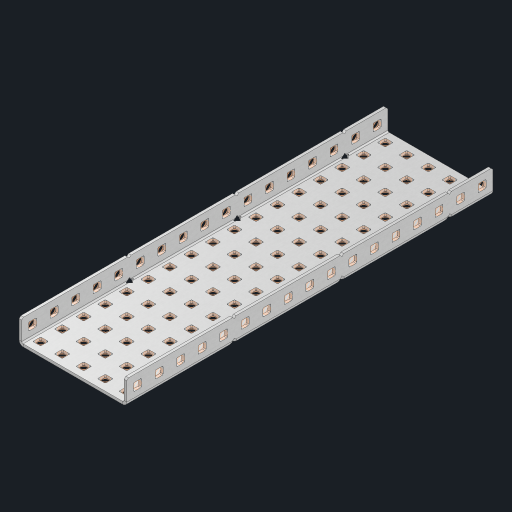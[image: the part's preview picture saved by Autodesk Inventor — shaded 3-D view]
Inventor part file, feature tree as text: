
AUTODESK INVENTOR PART (.ipt)
format: ipt  version: 2023 (Build 270158000, 158)  size: 1,488,896 bytes
history: native  units: in
note: dims shown in document units (in); Inventor stores cm internally (conversion verified against a paired STEP export)
features: other x124, extrude x118, sheet_metal_op x10, sketch x8, mirror x1, pattern_linear x1, chamfer x1
ambient origin geometry x8: Origin, YZ Plane, XZ Plane, XY Plane, X Axis, Y Axis, Z Axis, Center Point
bodies: Solid1 (feature_tree), Body (feature_tree)
feature tree (263):
  other  "Flange Pattern Plane"
  sheet_metal_op  "Flange Pattern"
  sheet_metal_op  "Body Pattern"
  other  "Arc Length"
  mirror  "Notch Mirror"
  pattern_linear  "Notch Pattern"  Spacing1=0.25in  [1 undecoded]
  chamfer  "End Chamfer"
  extrude  "Half Cut"  Depth=0.0625in
  sketch  "Sketch1"  dims[d0=2.5in]
  other  "Plate1"
  sketch  "Sketch2"  dims[d1=8.5in]
  other  "Plate2"
  sheet_metal_op  "Bend1"
  sheet_metal_op  "Corner1"
  sketch  "Sketch3"  dims[d2=0.0625in]
  other  "Flange Pattern Sketch"
  sketch  "Sketch7"  dims[d3=0.0625in]
  other  "Srf1"
  other  "Srf2"
  sketch  "Sketch8"  dims[d4=0.0312in]
  sketch  "Sketch9"  dims[d5=0.125in]
  other  "Srf91"
  sheet_metal_op  "Body Pattern Sketch"
  other  "Srf92"
  sketch  "Sketch13"  dims[d6=0.0625in]
  sketch  "Sketch14"  dims[d7=0.5in d8=90.0deg d9=0.0312in d10=0.25in d11=0.0625in d12=0.0625in d16=0.182in d17=0.02in d18=0.0625in d19=0.0in d20=0.25in d21=0.25in d46=0.172in d47=1.0in d48=0.0in d49=0.182in d50=0.02in d51=0.25in d52=0.25in d53=0.0625in d54=0.0in d55=0.172in d56=1.0in d57=0.0in d60=6.6929in d62=0.5in d63=1.9685in d65=0.5in d85=0.1473in d86=0.1782in d88=0.04in d89=0.0625in d90=0.0in d91=0.04in d92=0.0491in d95=2.5in d96=0.04in d97=0.25in d98=45.0deg d101=0.0in d102=2.497in d131=2.5in d132=6.6929in d134=0.5in d139=0.5in]
  other  "Srf856"
  other  "Srf1310"
  other  "Srf1311"
  other  "Srf1312"
  other  "Srf1376"
  other  "Srf1377"
  other  "Srf1728"
  other  "Srf1755"
  other  "Srf1878"
  other  "Srf1879"
  other  "Srf1880"
  other  "Srf1881"
  other  "Srf1882"
  other  "Srf1883"
  other  "Srf1884"
  other  "Srf1885"
  other  "Srf1886"
  other  "Srf1887"
  other  "Srf1888"
  other  "Srf1889"
  other  "Srf1890"
  other  "Srf1891"
  other  "Srf1892"
  other  "Srf1893"
  other  "Srf1894"
  other  "Srf1895"
  other  "Srf1896"
  other  "Srf1897"
  other  "Srf1898"
  other  "Srf1899"
  other  "Srf1900"
  other  "Srf1901"
  other  "Srf1902"
  other  "Srf1903"
  other  "Srf1904"
  other  "Srf1905"
  other  "Srf1942"
  other  "Srf1943"
  other  "Srf1944"
  other  "Srf1945"
  other  "Srf1946"
  other  "Srf1947"
  other  "Srf1948"
  other  "Srf1949"
  other  "Srf1950"
  other  "Srf1951"
  other  "Srf1952"
  other  "Srf1953"
  other  "Srf1954"
  other  "Srf1955"
  other  "Srf1956"
  other  "Srf1957"
  other  "Srf1958"
  other  "Srf1959"
  other  "Srf1960"
  other  "Srf1961"
  other  "Srf1962"
  other  "Srf1963"
  other  "Srf1964"
  other  "Srf1965"
  other  "Srf1966"
  other  "Srf1967"
  other  "Srf1968"
  other  "Srf1969"
  other  "Srf1970"
  other  "Srf2146"
  other  "Srf2147"
  other  "Srf2148"
  other  "Srf2149"
  other  "Srf2150"
  other  "Srf2151"
  other  "Srf2152"
  other  "Srf2153"
  other  "Srf2154"
  other  "Srf2155"
  other  "Srf2156"
  other  "Srf2157"
  other  "Srf2158"
  other  "Srf2159"
  other  "Srf2160"
  other  "Srf2161"
  other  "Srf2162"
  other  "Srf2163"
  other  "Srf2164"
  other  "Srf2165"
  other  "Srf2166"
  other  "Srf2167"
  other  "Srf2168"
  other  "Srf2169"
  other  "Srf2170"
  other  "Srf2171"
  other  "Srf2172"
  other  "Srf2173"
  other  "Srf2174"
  other  "Srf2175"
  other  "Srf2176"
  other  "Srf2177"
  other  "Srf2178"
  other  "Srf2179"
  other  "Srf2180"
  other  "Srf2181"
  other  "Srf2182"
  other  "Srf2183"
  other  "Srf2184"
  other  "Srf2185"
  other  "Srf2186"
  other  "Srf2187"
  other  "Srf2188"
  other  "Srf2189"
  other  "Srf2190"
  other  "Srf2191"
  other  "Srf2192"
  other  "Srf2193"
  other  "Srf2194"
  other  "Srf2195"
  sheet_metal_op  "Flange Stamp"
  sheet_metal_op  "Flange Circle"
  sheet_metal_op  "Body Stamp"
  sheet_metal_op  "Body Circle"
  sheet_metal_op  "Notch"
  extrude  "ExtrusionSrf2"  Depth=0.0625in
  extrude  "ExtrusionSrf92"  Depth=2.5in
  extrude  "ExtrusionSrf856"  Depth=0.02in
  extrude  "ExtrusionSrf1310"  Depth=0.0625in
  extrude  "ExtrusionSrf1311"  TaperAngle=0.0deg  [1 undecoded]
  extrude  "ExtrusionSrf1312"  Depth=0.25in
  extrude  "ExtrusionSrf1376"  Depth=0.25in
  extrude  "ExtrusionSrf1377"  Depth=2.5in
  extrude  "ExtrusionSrf1728"  Depth=2.5in TaperAngle=0.0deg
  extrude  "ExtrusionSrf1755"  Depth=2.5in
  extrude  "ExtrusionSrf1878"  Depth=0.02in
  extrude  "ExtrusionSrf1879"  Depth=0.25in
  extrude  "ExtrusionSrf1880"  Depth=0.25in
  extrude  "ExtrusionSrf1881"  Depth=0.0625in
  extrude  "ExtrusionSrf1882"  TaperAngle=0.0deg  [1 undecoded]
  extrude  "ExtrusionSrf1883"  Depth=2.5in
  extrude  "ExtrusionSrf1884"  Depth=2.5in TaperAngle=0.0deg
  extrude  "ExtrusionSrf1885"  Depth=2.5in
  extrude  "ExtrusionSrf1886"  Depth=2.5in
  extrude  "ExtrusionSrf1887"  Depth=2.5in
  extrude  "ExtrusionSrf1888"  Depth=2.5in
  extrude  "ExtrusionSrf1889"  Depth=2.5in
  extrude  "ExtrusionSrf1890"  Depth=0.0625in
  extrude  "ExtrusionSrf1891"  TaperAngle=0.0deg  [1 undecoded]
  extrude  "ExtrusionSrf1892"  Depth=2.5in
  extrude  "ExtrusionSrf1893"  Depth=2.5in
  extrude  "ExtrusionSrf1894"  Depth=2.5in
  extrude  "ExtrusionSrf1895"  Depth=0.25in TaperAngle=45.0deg
  extrude  "ExtrusionSrf1896"  TaperAngle=0.0deg  [1 undecoded]
  extrude  "ExtrusionSrf1897"  Depth=2.5in
  extrude  "ExtrusionSrf1898"  Depth=2.5in
  extrude  "ExtrusionSrf1899"  Depth=2.5in
  extrude  "ExtrusionSrf1900"  Depth=2.5in
  extrude  "ExtrusionSrf1901"  Depth=2.5in
  extrude  "ExtrusionSrf1902"  [1 undecoded]
  extrude  "ExtrusionSrf1903"  [1 undecoded]
  extrude  "ExtrusionSrf1904"  [1 undecoded]
  extrude  "ExtrusionSrf1905"  [1 undecoded]
  extrude  "ExtrusionSrf1942"  [1 undecoded]
  extrude  "ExtrusionSrf1943"  [1 undecoded]
  extrude  "ExtrusionSrf1944"  [1 undecoded]
  extrude  "ExtrusionSrf1945"  [1 undecoded]
  extrude  "ExtrusionSrf1946"  [1 undecoded]
  extrude  "ExtrusionSrf1947"  [1 undecoded]
  extrude  "ExtrusionSrf1948"  [1 undecoded]
  extrude  "ExtrusionSrf1949"  [1 undecoded]
  extrude  "ExtrusionSrf1950"  [1 undecoded]
  extrude  "ExtrusionSrf1951"  [1 undecoded]
  extrude  "ExtrusionSrf1952"  [1 undecoded]
  extrude  "ExtrusionSrf1953"  [1 undecoded]
  extrude  "ExtrusionSrf1954"  [1 undecoded]
  extrude  "ExtrusionSrf1955"  [1 undecoded]
  extrude  "ExtrusionSrf1956"  [1 undecoded]
  extrude  "ExtrusionSrf1957"  [1 undecoded]
  extrude  "ExtrusionSrf1958"  [1 undecoded]
  extrude  "ExtrusionSrf1959"  [1 undecoded]
  extrude  "ExtrusionSrf1960"  [1 undecoded]
  extrude  "ExtrusionSrf1961"  [1 undecoded]
  extrude  "ExtrusionSrf1962"  [1 undecoded]
  extrude  "ExtrusionSrf1963"  [1 undecoded]
  extrude  "ExtrusionSrf1964"  [1 undecoded]
  extrude  "ExtrusionSrf1965"  [1 undecoded]
  extrude  "ExtrusionSrf1966"  [1 undecoded]
  extrude  "ExtrusionSrf1967"  [1 undecoded]
  extrude  "ExtrusionSrf1968"  [1 undecoded]
  extrude  "ExtrusionSrf1969"  [1 undecoded]
  extrude  "ExtrusionSrf1970"  [1 undecoded]
  extrude  "ExtrusionSrf2146"  [1 undecoded]
  extrude  "ExtrusionSrf2147"  [1 undecoded]
  extrude  "ExtrusionSrf2148"  [1 undecoded]
  extrude  "ExtrusionSrf2149"  [1 undecoded]
  extrude  "ExtrusionSrf2150"  [1 undecoded]
  extrude  "ExtrusionSrf2151"  [1 undecoded]
  extrude  "ExtrusionSrf2152"  [1 undecoded]
  extrude  "ExtrusionSrf2153"  [1 undecoded]
  extrude  "ExtrusionSrf2154"  [1 undecoded]
  extrude  "ExtrusionSrf2155"  [1 undecoded]
  extrude  "ExtrusionSrf2156"  [1 undecoded]
  extrude  "ExtrusionSrf2157"  [1 undecoded]
  extrude  "ExtrusionSrf2158"  [1 undecoded]
  extrude  "ExtrusionSrf2159"  [1 undecoded]
  extrude  "ExtrusionSrf2160"  [1 undecoded]
  extrude  "ExtrusionSrf2161"  [1 undecoded]
  extrude  "ExtrusionSrf2162"  [1 undecoded]
  extrude  "ExtrusionSrf2163"  [1 undecoded]
  extrude  "ExtrusionSrf2164"  [1 undecoded]
  extrude  "ExtrusionSrf2165"  [1 undecoded]
  extrude  "ExtrusionSrf2166"  [1 undecoded]
  extrude  "ExtrusionSrf2167"  [1 undecoded]
  extrude  "ExtrusionSrf2168"  [1 undecoded]
  extrude  "ExtrusionSrf2169"  [1 undecoded]
  extrude  "ExtrusionSrf2170"  [1 undecoded]
  extrude  "ExtrusionSrf2171"  [1 undecoded]
  extrude  "ExtrusionSrf2172"  [1 undecoded]
  extrude  "ExtrusionSrf2173"  [1 undecoded]
  extrude  "ExtrusionSrf2174"  [1 undecoded]
  extrude  "ExtrusionSrf2175"  [1 undecoded]
  extrude  "ExtrusionSrf2176"  [1 undecoded]
  extrude  "ExtrusionSrf2177"  [1 undecoded]
  extrude  "ExtrusionSrf2178"  [1 undecoded]
  extrude  "ExtrusionSrf2179"  [1 undecoded]
  extrude  "ExtrusionSrf2180"  [1 undecoded]
  extrude  "ExtrusionSrf2181"  [1 undecoded]
  extrude  "ExtrusionSrf2182"  [1 undecoded]
  extrude  "ExtrusionSrf2183"  [1 undecoded]
  extrude  "ExtrusionSrf2184"  [1 undecoded]
  extrude  "ExtrusionSrf2185"  [1 undecoded]
  extrude  "ExtrusionSrf2186"  [1 undecoded]
  extrude  "ExtrusionSrf2187"  [1 undecoded]
  extrude  "ExtrusionSrf2188"  [1 undecoded]
  extrude  "ExtrusionSrf2189"  [1 undecoded]
  extrude  "ExtrusionSrf2190"  [1 undecoded]
  extrude  "ExtrusionSrf2191"  [1 undecoded]
  extrude  "ExtrusionSrf2192"  [1 undecoded]
  extrude  "ExtrusionSrf2193"  [1 undecoded]
  extrude  "ExtrusionSrf2194"  [1 undecoded]
  extrude  "ExtrusionSrf2195"  [1 undecoded]
note: 88 required parameter values undecoded (feature->parameter linkage not recoverable at this tier; creation-order binding heuristic only, values carry confidence <= 0.55)
